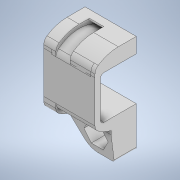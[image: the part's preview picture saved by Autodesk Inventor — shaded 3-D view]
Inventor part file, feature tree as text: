
AUTODESK INVENTOR PART (.ipt)
format: ipt  version: 2022.3 (Build 263350000, 350)  size: 1,253,376 bytes
history: native  units: mm
features: extrude x44, projected_geometry x43, sketch x31, fillet x3, mirror x2, plane x2
ambient origin geometry x8: Origin, YZ Plane, XZ Plane, XY Plane, X Axis, Y Axis, Z Axis, Center Point
bodies: Solid1 (feature_tree)
feature tree (125):
  extrude  "Extrusion1"  Depth=0.6mm
  extrude  "Extrusion2"  Depth=5.1mm
  extrude  "Extrusion3"  Depth=2.0mm TaperAngle=0.0deg
  extrude  "Extrusion4"  Depth=1.0mm
  extrude  "Extrusion5"  Depth=2.5mm TaperAngle=0.0deg
  mirror  "Mirror1"
  extrude  "Extrusion6"  Depth=30.0mm TaperAngle=0.0deg
  extrude  "Extrusion7"  Depth=3.5mm
  extrude  "Extrusion8"  Depth=37.5mm
  extrude  "Extrusion9"  Depth=1.5mm
  extrude  "Extrusion10"  Depth=4.0mm TaperAngle=0.0deg
  fillet  "Fillet1"  Radius=2.75mm
  extrude  "Extrusion11"  Depth=2.7mm
  sketch  "Sketch13"  dims[d37=2.0mm d38=0.0mm d39=3.0mm d40=0.0mm]
  extrude  "Extrusion12"  Depth=2.0mm TaperAngle=0.0deg
  extrude  "Extrusion13"  Depth=0.5mm
  extrude  "Extrusion14"  Depth=5.0mm
  extrude  "Extrusion15"  Depth=2.0mm TaperAngle=0.0deg
  extrude  "Extrusion16"  Depth=5.0mm
  extrude  "Extrusion17"  Depth=2.0mm
  extrude  "Extrusion18"  Depth=14.25mm TaperAngle=0.0deg
  sketch  "Sketch14"  dims[d41=7.0mm d42=0.0mm d43=0.5mm]
  extrude  "Extrusion19"  Depth=14.25mm TaperAngle=0.0deg
  extrude  "Extrusion20"  Depth=14.25mm TaperAngle=0.0deg
  plane  "Work Plane1"
  extrude  "Extrusion21"  Depth=2.5mm TaperAngle=0.0deg
  extrude  "Extrusion22"  Depth=4.0mm TaperAngle=0.0deg
  sketch  "Sketch17"  dims[d49=30.4mm d52=5.0mm]
  extrude  "Extrusion23"  Depth=14.25mm TaperAngle=0.0deg
  extrude  "Extrusion24"  Depth=14.25mm TaperAngle=0.0deg
  extrude  "Extrusion25"  Depth=2.0mm TaperAngle=0.0deg
  fillet  "Fillet3"  Radius=0.5mm
  extrude  "Extrusion26"  Depth=10.0mm TaperAngle=0.0deg
  extrude  "Extrusion27"  TaperAngle=0.0deg  [1 undecoded]
  extrude  "Extrusion28"  TaperAngle=0.0deg  [1 undecoded]
  extrude  "Extrusion29"  Depth=3.0mm TaperAngle=0.0deg
  extrude  "Extrusion30"  TaperAngle=0.0deg  [1 undecoded]
  sketch  "Sketch24"  dims[d75=2.5mm d76=0.0mm d77=14.25mm d78=0.0mm]
  extrude  "Extrusion31"  Depth=10.0mm TaperAngle=0.0deg
  extrude  "Extrusion32"  Depth=10.0mm TaperAngle=0.0deg
  sketch  "Sketch25"  dims[d79=14.25mm d80=0.0mm d82=14.25mm d83=0.0mm]
  extrude  "Extrusion33"  Depth=0.2mm TaperAngle=0.0deg
  extrude  "Extrusion34"  Depth=0.2mm TaperAngle=0.0deg
  extrude  "Extrusion35"  Depth=0.2mm TaperAngle=0.0deg
  extrude  "Extrusion36"  Depth=0.2mm
  sketch  "Sketch26"  dims[d84=2.0mm d85=14.25mm d86=0.0mm d87=0.5mm]
  extrude  "Extrusion37"  TaperAngle=0.0deg  [1 undecoded]
  extrude  "Extrusion38"  Depth=0.2mm TaperAngle=0.0deg
  extrude  "Extrusion39"  Depth=0.2mm TaperAngle=0.0deg
  extrude  "Extrusion40"  [1 undecoded]
  mirror  "Mirror2"
  extrude  "Extrusion41"  [1 undecoded]
  fillet  "Fillet4"  [1 undecoded]
  extrude  "Extrusion42"  [1 undecoded]
  extrude  "Extrusion43"  [1 undecoded]
  extrude  "Extrusion44"  [1 undecoded]
  sketch  "Sketch1"  dims[d0=11.5mm d1=0.0mm d2=0.6mm]
  sketch  "Sketch2"  dims[d3=0.7mm d4=5.1mm]
  projected_geometry  "Projected Loop1"
  projected_geometry  "Projected Loop2"
  sketch  "Sketch3"  dims[d5=2.0mm d6=11.5mm d7=0.0mm]
  sketch  "Sketch4"  dims[d8=1.0mm d9=1.0mm]
  sketch  "Sketch6"  dims[d10=1.0mm d11=2.5mm d12=0.0mm]
  projected_geometry  "Projected Loop3"
  sketch  "Sketch7"  dims[d13=0.1mm d14=0.0mm d21=30.0mm d22=0.0mm]
  projected_geometry  "Projected Loop4"
  projected_geometry  "Projected Loop5"
  projected_geometry  "Projected Loop6"
  sketch  "Sketch8"  dims[d23=44.0mm d24=3.5mm]
  projected_geometry  "Projected Loop7"
  projected_geometry  "Projected Loop8"
  sketch  "Sketch9"  dims[d25=3.0mm d27=37.5mm]
  projected_geometry  "Projected Loop9"
  sketch  "Sketch10"  dims[d28=1.5mm d29=1.5mm]
  projected_geometry  "Projected Loop10"
  sketch  "Sketch11"  dims[d30=3.0mm d31=4.0mm d32=0.0mm d33=2.75mm d34=0.0mm]
  projected_geometry  "Projected Loop11"
  sketch  "Sketch12"  dims[d35=2.7mm d36=2.7mm]
  projected_geometry  "Projected Loop12"
  projected_geometry  "Projected Loop13"
  projected_geometry  "Projected Loop14"
  projected_geometry  "Projected Loop15"
  projected_geometry  "Projected Loop16"
  projected_geometry  "Projected Loop17"
  projected_geometry  "Projected Loop18"
  sketch  "Sketch15"  dims[d44=31.0mm d45=5.0mm]
  sketch  "Sketch16"  dims[d46=3.0mm d47=2.0mm d48=0.0mm]
  projected_geometry  "Projected Loop19"
  projected_geometry  "Projected Loop20"
  projected_geometry  "Projected Loop21"
  projected_geometry  "Projected Loop22"
  sketch  "Sketch18"  dims[d53=2.0mm d54=1.0mm]
  projected_geometry  "Projected Loop23"
  sketch  "Sketch19"  dims[d55=15.0mm d56=0.0mm d57=14.25mm d58=0.0mm]
  projected_geometry  "Projected Loop24"
  projected_geometry  "Projected Loop25"
  sketch  "Sketch20"  dims[d59=14.25mm d60=0.0mm d61=14.25mm d62=0.0mm]
  projected_geometry  "Projected Loop26"
  sketch  "Sketch21"  dims[d63=14.25mm d64=0.0mm d65=14.25mm d66=0.0mm]
  projected_geometry  "Projected Loop27"
  projected_geometry  "Projected Loop28"
  sketch  "Sketch22"  dims[d67=2.5mm d68=0.0mm d69=2.5mm d70=0.0mm]
  projected_geometry  "Projected Loop29"
  sketch  "Sketch23"  dims[d71=2.5mm d72=0.0mm d73=4.0mm d74=0.0mm]
  projected_geometry  "Projected Loop30"
  projected_geometry  "Projected Loop31"
  projected_geometry  "Projected Loop32"
  projected_geometry  "Projected Loop33"
  projected_geometry  "Projected Loop34"
  projected_geometry  "Projected Loop35"
  projected_geometry  "Projected Loop36"
  sketch  "Sketch27"  dims[d88=0.0mm d89=0.0mm d90=10.0mm d91=0.0mm]
  projected_geometry  "Projected Loop37"
  sketch  "Sketch28"  dims[d92=0.0mm d93=0.0mm d94=0.0mm d95=0.0mm]
  projected_geometry  "Projected Loop38"
  plane  "Work Plane2"
  sketch  "Sketch29"  dims[d96=1.0mm d97=0.0mm d98=0.0mm d99=0.0mm]
  projected_geometry  "Projected Loop39"
  sketch  "Sketch30"  dims[d100=8.0mm d101=0.0mm d102=3.0mm d103=0.0mm]
  projected_geometry  "Projected Loop40"
  projected_geometry  "Projected Loop41"
  sketch  "Sketch31"  dims[d104=1.75mm d105=2.25mm d106=0.0mm d107=0.0mm d108=0.0mm d109=0.0mm]
  projected_geometry  "Projected Loop42"
  projected_geometry  "Projected Loop43"
  sketch  "Sketch32"  dims[d110=3.5mm d111=10.0mm d112=0.0mm d113=10.0mm d114=0.0mm d115=1.0mm d116=0.0mm d117=7.5mm d118=0.0mm d119=7.5mm d120=0.0mm d121=0.2mm d122=0.0mm d123=0.0mm d124=6.0mm d125=0.0mm d126=20.0mm d127=0.0mm]
note: 10 required parameter values undecoded (feature->parameter linkage not recoverable at this tier; creation-order binding heuristic only, values carry confidence <= 0.55)
